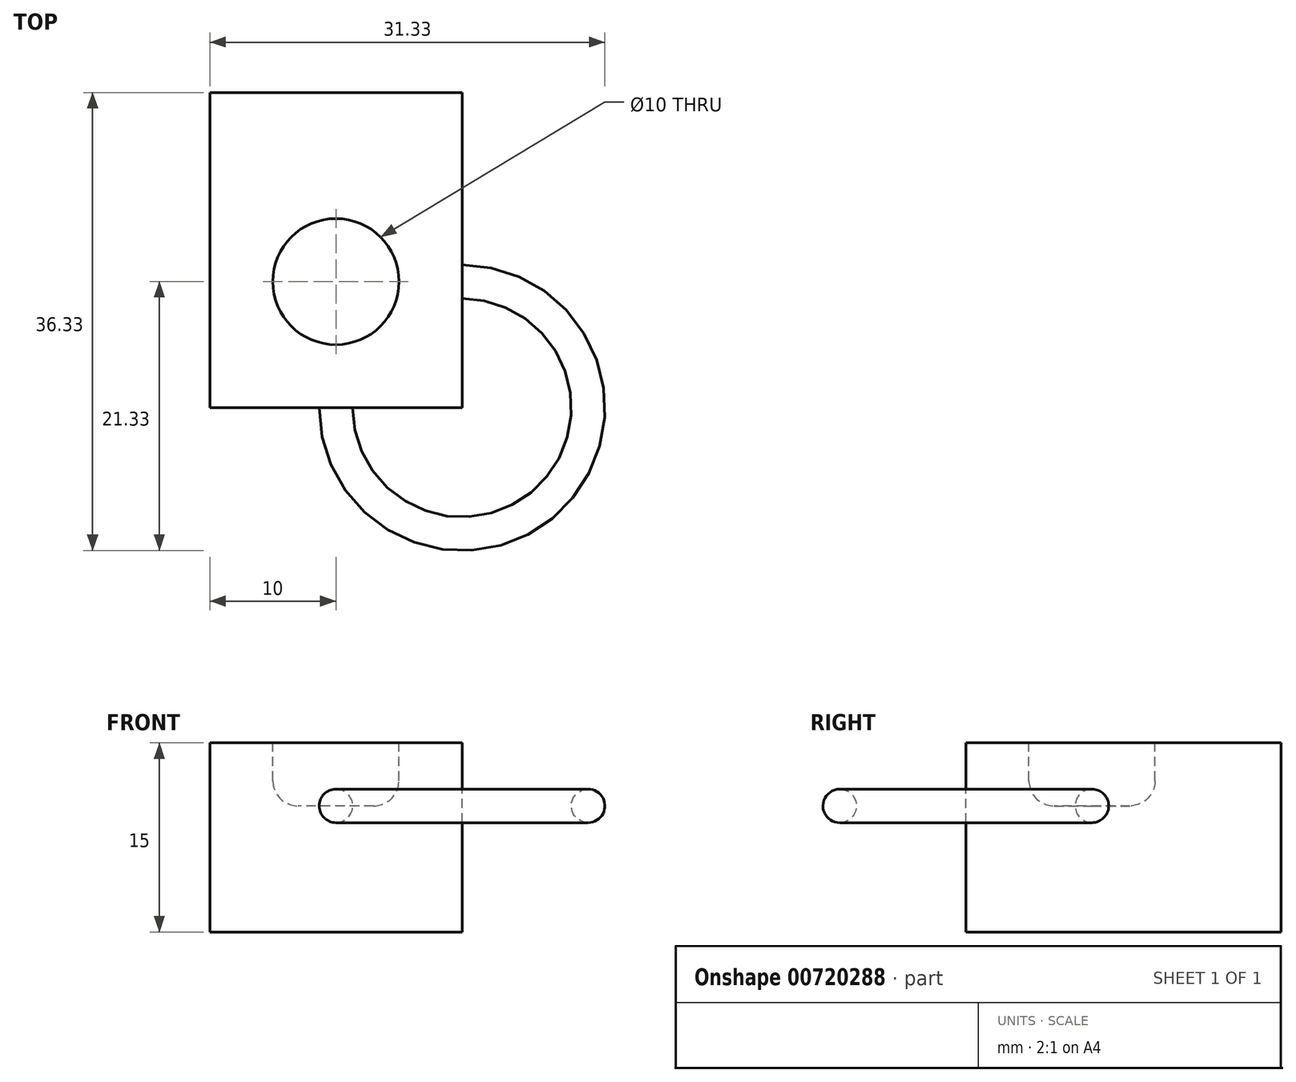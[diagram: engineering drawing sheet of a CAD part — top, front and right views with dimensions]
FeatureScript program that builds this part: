
annotation { "Feature Type Name" : "Feature", "Feature Type Description" : "" }
export const myFeature = defineFeature(function(context is Context, id is Id, definition is map)
    precondition{}
    {
        {
            var Q0;
            Q0=qCreatedBy(makeId("Front.planeOp"),FACE);
            var sketch = newSketch(context, id + "F0", { "sketchPlane" : qUnion([Q0])});
            skLineSegment(sketch, "E0.bottom", {"start": v(0, 0) * mm, "end": v(20, 0) * mm});
            skLineSegment(sketch, "E0.top", {"start": v(0, 15) * mm, "end": v(20, 15) * mm});
            skLineSegment(sketch, "E0.left", {"start": v(0, 0) * mm, "end": v(0, 15) * mm});
            skLineSegment(sketch, "E0.right", {"start": v(20, 0) * mm, "end": v(20, 15) * mm});
            skSolve(sketch);
        }
        {
            var Q0;
            Q0 = qSketchRegion(id + "F0", true);
            var Q1;
            Q1 = qConstructionFilter(qBodyType(qCreatedBy(id + "F0" ,EDGE), BodyType.WIRE), ConstructionObject.NO);
            extrude(context, id + "F1", {"entities" : qUnion([Q0]), "surfaceEntities" : qUnion([Q1]), "depth" : 25 * mm, "offsetDistance" : 25 * mm});
        }
        {
            var Q0;
            Q0=makeQuery(id+"F1.opExtrude","SWEPT_FACE",FACE,{"disambiguationData":[OSD([sQuery(id+"F0.wireOp",EDGE,"E0.top")])]});
            var sketch = newSketch(context, id + "F2", { "sketchPlane" : qUnion([Q0])});
            skCircle(sketch, "E1", {"center": v(10, -15) * mm, "radius": 5 * mm});
            skSolve(sketch);
        }
        {
            var Q0;
            Q0 = qSketchRegion(id + "F2", true);
            extrude(context, id + "F3", {"entities" : qUnion([Q0]), "operationType" : NewBodyOperationType.REMOVE, "oppositeDirection" : true, "depth" : 5 * mm, "offsetDistance" : 25 * mm});
        }
        {
            var Q0;
            Q0=makeQuery(id+"F3.boolean.opBoolean","COPY",EDGE,{"derivedFrom":makeQuery(id+"F3.opExtrude","CAP_EDGE",EDGE,{"disambiguationData":[OSD([sQuery(id+"F2.wireOp",EDGE,"E1")])],"isStart":false})});
            fillet(context, id + "F4", {"entities" : qUnion([Q0]), "radius" : 2 * mm, "tangentPropagation" : true, "allowEdgeOverflow" : false});
        }
        {
            var Q0;
            Q0=makeQuery(id+"F1.opExtrude","CAP_FACE",FACE,{"disambiguationData":[OSD([sQuery(id+"F0.wireOp",EDGE,"E0.bottom"),sQuery(id+"F0.wireOp",EDGE,"E0.top"),sQuery(id+"F0.wireOp",EDGE,"E0.left"),sQuery(id+"F0.wireOp",EDGE,"E0.right")])],"isStart":false});
            var sketch = newSketch(context, id + "F5", { "sketchPlane" : qUnion([Q0])});
            skCircle(sketch, "E2", {"center": v(10, 10) * mm, "radius": 1.33 * mm});
            skSolve(sketch);
        }
        {
            var Q0;
            Q0 = qSketchRegion(id + "F5", true);
            var Q1;
            Q1=makeQuery(id+"F1.opExtrude","CAP_EDGE",EDGE,{"disambiguationData":[OSD([sQuery(id+"F0.wireOp",EDGE,"E0.right")])],"isStart":false});
            revolve(context, id + "F6", {"surfaceOperationType" : NewSurfaceOperationType.NEW, "entities" : qUnion([Q0]), "axis" : qUnion([Q1]), "revolveType" : RevolveType.ONE_DIRECTION, "angle" : 270 * degree});
        }
    });
